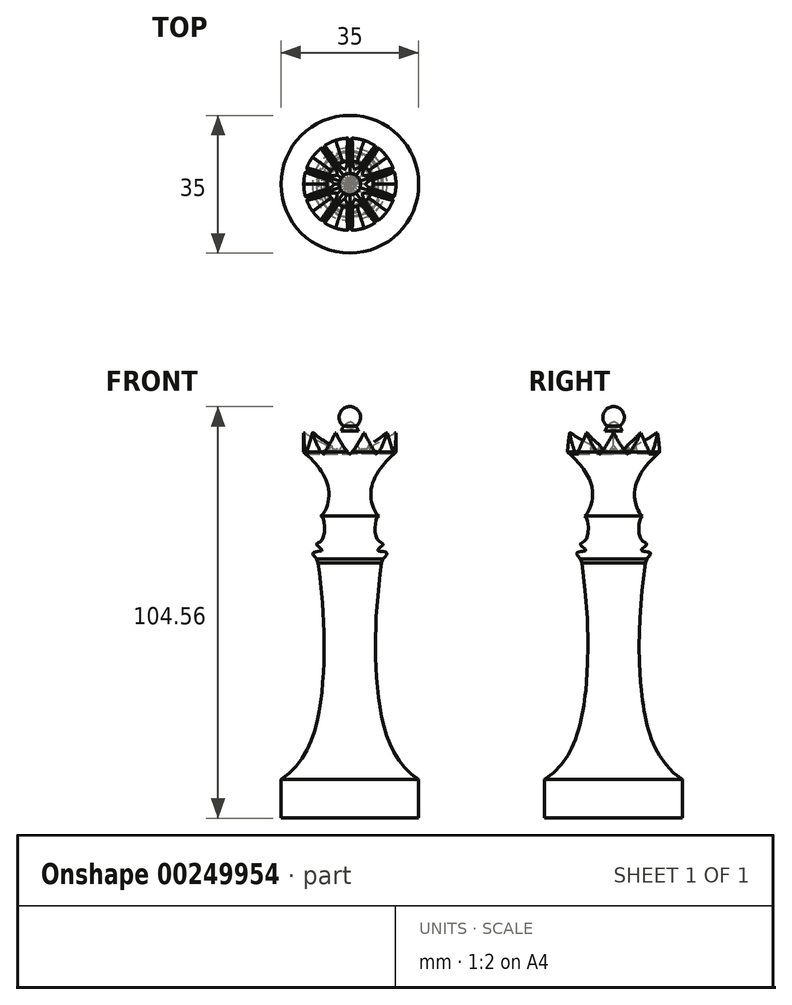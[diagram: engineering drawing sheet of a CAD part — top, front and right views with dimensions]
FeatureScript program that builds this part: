
annotation { "Feature Type Name" : "Feature", "Feature Type Description" : "" }
export const myFeature = defineFeature(function(context is Context, id is Id, definition is map)
    precondition{}
    {
        {
            var Q0;
            Q0=qCreatedBy(makeId("Front.planeOp"),FACE);
            var sketch = newSketch(context, id + "F0", { "sketchPlane" : qUnion([Q0])});
            skLineSegment(sketch, "E0.bottom", {"start": v(17.5, -38.2) * mm, "end": v(-17.5, -38.2) * mm});
            skLineSegment(sketch, "E0.top", {"start": v(17.5, -48) * mm, "end": v(-17.5, -48) * mm});
            skLineSegment(sketch, "E0.left", {"start": v(17.5, -38.2) * mm, "end": v(17.5, -48) * mm});
            skLineSegment(sketch, "E0.right", {"start": v(-17.5, -38.2) * mm, "end": v(-17.5, -48) * mm});
            skPoint(sketch, "E0.middle", {"position": v(0, -43.1) * mm});
            skFitSpline(sketch, "E1", {"points": [v(-7.36, 28.76) * mm, v(-5.32, 33.96) * mm, v(-11.71, 45) * mm], "startDerivative": vector(7.16, 4.27) * mm, "endDerivative": vector(-22.2, 18.85) * mm});
            skFitSpline(sketch, "E2", {"points": [v(-11.71, 45) * mm, v(-3.82, 46.1) * mm, v(0, 52.66) * mm], "startDerivative": vector(29.35, 3.67) * mm, "endDerivative": vector(14.39, 2.02) * mm});
            skCircle(sketch, "E3", {"center": v(0, 53.83) * mm, "radius": 2.73 * mm});
            skLineSegment(sketch, "E4", {"start": v(0, 67.44) * mm, "end": v(0, -61.2) * mm});
            skLineSegment(sketch, "E5.bottom", {"start": v(-11.71, 45) * mm, "end": v(-5.87, 45) * mm});
            skLineSegment(sketch, "E5.top", {"start": v(-11.71, 49.86) * mm, "end": v(-5.87, 49.86) * mm});
            skLineSegment(sketch, "E5.left", {"start": v(-11.71, 45) * mm, "end": v(-11.71, 49.86) * mm});
            skLineSegment(sketch, "E5.right", {"start": v(-5.87, 45) * mm, "end": v(-5.87, 49.86) * mm});
            skFitSpline(sketch, "E6", {"points": [v(-8.42, 17.84) * mm, v(-9.43, 19.31) * mm, v(-7.1, 20.03) * mm, v(-8.42, 21.53) * mm, v(-7.02, 22.79) * mm, v(-7.36, 28.76) * mm], "startDerivative": vector(4.39, 0) * mm, "endDerivative": vector(-10.91, 4.17) * mm});
            skFitSpline(sketch, "E7", {"points": [v(-8.18, 17.84) * mm, v(-7.02, -14.9) * mm, v(-17.5, -38.2) * mm], "startDerivative": vector(9.42, -66.82) * mm, "endDerivative": vector(-48.61, -31.62) * mm});
            skLineSegment(sketch, "E8", {"start": v(-8.42, 17.84) * mm, "end": v(-8.03, 16.81) * mm});
            skLineSegment(sketch, "E9", {"start": v(-8.42, 17.84) * mm, "end": v(-8.49, 18) * mm});
            skSolve(sketch);
        }
        {
            var Q0;
            {var subQ8=sQuery(id+"F0.wireOp",EDGE,"2535b165-8c30-4f96-9e35-496b200d8c39");Q0=makeQuery(id+"F0.imprint","IMPRINT",FACE,{"disambiguationData":[TD([[makeQuery(id+"F0.imprint","IMPRINT",EDGE,{"derivedFrom":subQ8}),-1.0]])]});}
            var Q1;
            {var subQ0=sQuery(id+"F0.wireOp",EDGE,"p2Q5Cg4Y-M3Bh-73iV-2hDV-Me0pNQYj1xe1");var subQ1=makeQuery(id+"F0.imprint","INTERSECT",VERTEX,{"derivedFrom":[subQ0,sQuery(id+"F0.wireOp",EDGE,"56d9c8e5-4a78-4b27-bc3c-4339a85488de")]});Q1=makeQuery(id+"F0.imprint","IMPRINT",FACE,{"disambiguationData":[TD([[makeQuery(id+"F0.imprint","IMPRINT",EDGE,{"disambiguationData":[TD([[subQ1,1.0]])],"derivedFrom":subQ0}),1.0]])]});}
            var Q2;
            {var subQ0=sQuery(id+"F0.wireOp",EDGE,"WTfuDzib-b3Re-L3zW-bkWg-t948RWQyNecH");var subQ1=makeQuery(id+"F0.imprint","INTERSECT",VERTEX,{"derivedFrom":[subQ0,sQuery(id+"F0.wireOp",EDGE,"56d9c8e5-4a78-4b27-bc3c-4339a85488de")]});Q2=makeQuery(id+"F0.imprint","IMPRINT",FACE,{"disambiguationData":[TD([[makeQuery(id+"F0.imprint","IMPRINT",EDGE,{"disambiguationData":[TD([[subQ1,1.0]])],"derivedFrom":subQ0}),1.0]])]});}
            var Q3;
            {var subQ0=sQuery(id+"F0.wireOp",EDGE,"56d9c8e5-4a78-4b27-bc3c-4339a85488de");Q3=makeQuery(id+"F0.imprint","IMPRINT",FACE,{"disambiguationData":[TD([[makeQuery(id+"F0.imprint","IMPRINT",EDGE,{"derivedFrom":subQ0}),1.0]])]});}
            var Q4;
            {var subQ0=sQuery(id+"F0.wireOp",EDGE,"E0.right");Q4=makeQuery(id+"F0.imprint","IMPRINT",FACE,{"disambiguationData":[TD([[makeQuery(id+"F0.imprint","IMPRINT",EDGE,{"derivedFrom":subQ0}),1.0]])]});}
            var Q5;
            {var subQ0=sQuery(id+"F0.wireOp",EDGE,"E4");var subQ1=sQuery(id+"F0.wireOp",EDGE,"E2");var subQ2=makeQuery(id+"F0.imprint","INTERSECT",VERTEX,{"derivedFrom":[subQ1,subQ0]});Q5=makeQuery(id+"F0.imprint","IMPRINT",FACE,{"disambiguationData":[TD([[makeQuery(id+"F0.imprint","IMPRINT",EDGE,{"disambiguationData":[TD([[subQ2,1.0]])],"derivedFrom":subQ1}),1.0]])]});}
            var Q6;
            {var subQ0=sQuery(id+"F0.wireOp",EDGE,"56d9c8e5-4a78-4b27-bc3c-4339a85488de");var subQ1=sQuery(id+"F0.wireOp",EDGE,"WTfuDzib-b3Re-L3zW-bkWg-t948RWQyNecH");var subQ2=makeQuery(id+"F0.imprint","INTERSECT",VERTEX,{"disambiguationData":[OD(0.0)],"derivedFrom":[subQ1,subQ0]});Q6=makeQuery(id+"F0.imprint","IMPRINT",FACE,{"disambiguationData":[TD([[makeQuery(id+"F0.imprint","IMPRINT",EDGE,{"disambiguationData":[TD([[subQ2,1.0]])],"derivedFrom":subQ1}),1.0]])]});}
            var Q7;
            {var subQ4=sQuery(id+"F0.wireOp",EDGE,"E5.top");Q7=makeQuery(id+"F0.imprint","IMPRINT",FACE,{"disambiguationData":[TD([[makeQuery(id+"F0.imprint","IMPRINT",EDGE,{"derivedFrom":subQ4}),-1.0]])]});}
            var Q8;
            {var subQ0=sQuery(id+"F0.wireOp",EDGE,"56d9c8e5-4a78-4b27-bc3c-4339a85488de");var subQ1=sQuery(id+"F0.wireOp",EDGE,"p2Q5Cg4Y-M3Bh-73iV-2hDV-Me0pNQYj1xe1");var subQ2=makeQuery(id+"F0.imprint","INTERSECT",VERTEX,{"disambiguationData":[OD(1.0)],"derivedFrom":[subQ1,subQ0]});Q8=makeQuery(id+"F0.imprint","IMPRINT",FACE,{"disambiguationData":[TD([[makeQuery(id+"F0.imprint","IMPRINT",EDGE,{"disambiguationData":[TD([[subQ2,1.0]])],"derivedFrom":subQ1}),1.0]])]});}
            var Q9;
            Q9=makeQuery(id+"F0.imprint","IMPRINT",FACE,{"disambiguationData":[TD([[makeQuery(id+"F0.imprint","IMPRINT",EDGE,{"derivedFrom":sQuery(id+"F0.wireOp",EDGE,"e262b2d6-e077-4a59-af84-f3a4b3ec959b")}),-1.0]])]});
            var Q10;
            {var subQ13=sQuery(id+"F0.wireOp",EDGE,"E1");Q10=makeQuery(id+"F0.imprint","IMPRINT",FACE,{"disambiguationData":[TD([[makeQuery(id+"F0.imprint","IMPRINT",EDGE,{"derivedFrom":subQ13}),-1.0]])]});}
            var Q11;
            Q11=sQuery(id+"F0.wireOp",EDGE,"E4");
            revolve(context, id + "F1", {"entities" : qUnion([Q0, Q1, Q2, Q3, Q4, Q5, Q6, Q7, Q8, Q9, Q10]), "axis" : qUnion([Q11]), "revolveType" : RevolveType.FULL});
        }
        {
            var Q0;
            Q0=qCreatedBy(makeId("Front.planeOp"),FACE);
            var sketch = newSketch(context, id + "F2", { "sketchPlane" : qUnion([Q0])});
            skPoint(sketch, "E10.middle", {"position": v(0, 44.46) * mm});
            skFitSpline(sketch, "E11", {"points": [v(0, 44.46) * mm, v(-3.69, 50.33) * mm], "startDerivative": vector(-4, 3.56) * mm, "endDerivative": vector(-1.35, 4.32) * mm});
            skLineSegment(sketch, "E12", {"start": v(-3.69, 50.33) * mm, "end": v(0, 50.33) * mm});
            skLineSegment(sketch, "E13", {"start": v(0, 50.33) * mm, "end": v(0, 44.46) * mm});
            skLineSegment(sketch, "E14.bottom", {"start": v(-3.69, 50.33) * mm, "end": v(3.69, 50.33) * mm});
            skLineSegment(sketch, "E14.top", {"start": v(-3.69, 50.33) * mm, "end": v(3.69, 50.33) * mm});
            skLineSegment(sketch, "E14.left", {"start": v(-3.69, 50.33) * mm, "end": v(-3.69, 50.33) * mm});
            skLineSegment(sketch, "E14.right", {"start": v(3.69, 50.33) * mm, "end": v(3.69, 50.33) * mm});
            skPoint(sketch, "E14.middle", {"position": v(0, 50.33) * mm});
            skFitSpline(sketch, "E15", {"points": [v(3.69, 50.33) * mm, v(0, 44.46) * mm], "startDerivative": vector(-1.96, -4.53) * mm, "endDerivative": vector(-3.18, -3.23) * mm});
            skSolve(sketch);
        }
        {
            var Q0;
            Q0 = qSketchRegion(id + "F2", true);
            extrude(context, id + "F3", {"entities" : qUnion([Q0]), "endBound" : BoundingType.SYMMETRIC, "depth" : 30 * mm});
        }
        {
            var Q0;
            Q0=makeQuery(id+"F3.opExtrude","SWEPT_BODY",BODY,{"disambiguationData":[OSD([sQuery(id+"F2.wireOp",EDGE,"E11"),sQuery(id+"F2.wireOp",EDGE,"E14.top"),sQuery(id+"F2.wireOp",EDGE,"E15")])]});
            var Q1;
            Q1=sQuery(id+"F0.wireOp",EDGE,"E4");
            circularPattern(context, id + "F4", {"operationType" : NewBodyOperationType.REMOVE, "entities" : qUnion([Q0]), "axis" : qUnion([Q1]), "angle" : 360 * degree, "instanceCount" : 10, "equalSpace" : true});
        }
    });
